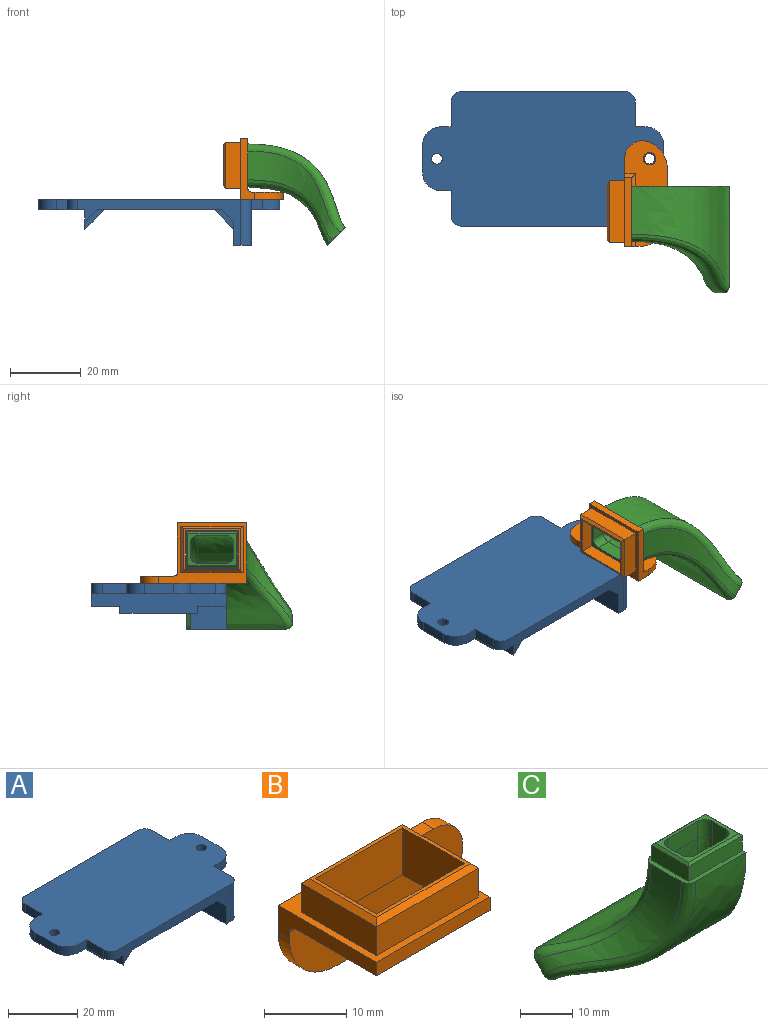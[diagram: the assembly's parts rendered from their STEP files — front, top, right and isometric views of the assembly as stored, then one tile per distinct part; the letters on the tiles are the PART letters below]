
ASSEMBLY  parts=3 mates=4
PART A: 41 faces, bbox 68x38x13 mm
  f0: plane 28x13mm, normal (0,0,-1), area 264.3mm2, adj f16,f17,f18,f19,f20,f21,f22,f23
  f1: plane 38x35mm, normal (0,0,-1), area 1242mm2, adj f2,f3,f13,f23,f29,f30,f31,f32
  f2: plane 8x3.5mm, normal (-0.71,0,-0.71), area 39.6mm2, adj f1,f23,f34,f37
  f3: plane 8x3.5mm, normal (0.71,0,-0.71), area 39.6mm2, adj f1,f23,f28,f31
  f4: plane 38x13mm, normal (0,0,-1), area 312.3mm2, adj f5,f6,f7,f8,f9,f10,f11,f12
  f5: plane 7x3mm, normal (-1,0,0), area 21mm2, adj f4,f6,f25,f27
  f6: plane 3x3mm, normal (0,1,0), area 9mm2, adj f4,f5,f7,f27
  f7: cylinder r=5mm len=5mm, axis (0,0,-1), area 23.6mm2, adj f4,f6,f8,f27
  f8: plane 8x3mm, normal (-1,0,0), area 24mm2, adj f4,f7,f9,f27
  f9: cylinder r=5mm len=5mm, axis (0,0,-1), area 23.6mm2, adj f4,f8,f10,f27
  f10: plane 3x3mm, normal (0,-1,0), area 9mm2, adj f4,f9,f11,f27
  f11: plane 7x3mm, normal (-1,0,0), area 21mm2, adj f4,f10,f12,f27
  f12: cylinder r=3mm len=3mm, axis (0,0,-1), area 14.1mm2, adj f4,f11,f13,f27
  f13: plane 46x13mm, normal (0,-1,0), area 170.2mm2, adj f1,f4,f12,f14,f27,f28,f29,f33
  f14: cylinder r=3mm len=13mm, axis (0,0,-1), area 61.3mm2, adj f13,f15,f27,f40
  f15: plane 13x7mm, normal (1,0,0), area 91mm2, adj f14,f16,f27,f39,f40
  f16: plane 3x3mm, normal (0,-1,0), area 9mm2, adj f0,f15,f17,f27
  f17: cylinder r=5mm len=5mm, axis (0,0,-1), area 23.6mm2, adj f0,f16,f18,f27
  f18: plane 8x3mm, normal (1,0,0), area 24mm2, adj f0,f17,f19,f27
  f19: cylinder r=5mm len=5mm, axis (0,0,-1), area 23.6mm2, adj f0,f18,f20,f27
  f20: plane 3x3mm, normal (0,1,0), area 9mm2, adj f0,f19,f21,f27
  f21: plane 7x3mm, normal (1,0,0), area 21mm2, adj f0,f20,f22,f27
  f22: cylinder r=3mm len=3mm, axis (0,0,-1), area 14.1mm2, adj f0,f21,f23,f27
  f23: plane 46x6.5mm, normal (0,1,0), area 150.3mm2, adj f0,f1,f2,f3,f4,f22,f25,f27
  f24: cylinder r=1.5mm len=3mm, axis (0,0,-1), area 28.3mm2, adj f0,f27
  f25: cylinder r=3mm len=3mm, axis (0,0,-1), area 14.1mm2, adj f4,f5,f23,f27
  f26: cylinder r=1.5mm len=3mm, axis (0,0,-1), area 28.3mm2, adj f4,f27
  f27: plane 68x38mm, normal (0,0,1), area 2220.7mm2, adj f5,f6,f7,f8,f9,f10,f11,f12
  f28: plane 38x5.5mm, normal (-1,0,0), area 177mm2, adj f3,f4,f13,f23,f29,f30,f31,f32
  f29: plane 8x3.5mm, normal (0.71,0,-0.71), area 39.6mm2, adj f1,f13,f28,f30
  f30: plane 5.5x5.5mm, normal (0,-1,0), area 9mm2, adj f1,f28,f29,f32
  f31: plane 5.5x5.5mm, normal (0,1,0), area 9mm2, adj f1,f3,f28,f32
  f32: plane 22x5.5mm, normal (0.71,0,-0.71), area 171.1mm2, adj f1,f28,f30,f31
  f33: plane 8x3.5mm, normal (-0.71,0,-0.71), area 39.6mm2, adj f1,f13,f36,f38
  f34: plane 28x5.5mm, normal (1,0,0), area 138mm2, adj f0,f2,f23,f35,f37,f39
  f35: plane 22x5.5mm, normal (-0.71,0,-0.71), area 171.1mm2, adj f1,f34,f36,f37,f38
  f36: plane 5.5x5.5mm, normal (0,-1,0), area 9mm2, adj f1,f33,f35,f38
  f37: plane 5.5x5.5mm, normal (0,1,0), area 9mm2, adj f1,f2,f34,f35
  f38: plane 10x6.5mm, normal (-1,0,0), area 61mm2, adj f13,f33,f35,f36,f39,f40
  f39: plane 10x5mm, normal (0,1,0), area 50mm2, adj f0,f15,f34,f38,f40
  f40: plane 10x5mm, normal (0,0,-1), area 48.1mm2, adj f13,f14,f15,f38,f39
PART B: 27 faces, bbox 29.8x17x17 mm
  f0: plane 17.5x4.3mm, normal (0,-1,0), area 75.3mm2, adj f1,f3,f9,f23
  f1: plane 13x4.3mm, normal (1,0,0), area 55.9mm2, adj f0,f2,f9,f21
  f2: plane 17.5x4.3mm, normal (0,1,0), area 75.3mm2, adj f1,f3,f9,f22
  f3: plane 13x4.3mm, normal (-1,0,0), area 55.9mm2, adj f0,f2,f9,f24
  f4: plane 16.1x11.6mm, normal (0,0,1), area 26.7mm2, adj f10,f11,f12,f13,f21,f22,f23,f24
  f5: plane 17x4mm, normal (-1,0,0), area 38.2mm2, adj f6,f8,f9,f14,f16,f18,f25
  f6: plane 19.5x2mm, normal (0,-1,0), area 39mm2, adj f5,f7,f8,f9
  f7: plane 14x2mm, normal (1,0,0), area 28mm2, adj f6,f8,f9,f26
  f8: plane 19.5x14mm, normal (0,0,-1), area 112.9mm2, adj f5,f6,f7,f10,f11,f12,f13,f25
  f9: plane 24.83x17mm, normal (0,0,1), area 114.9mm2, adj f0,f1,f2,f3,f5,f6,f7,f14
  f10: plane 15.1x7mm, normal (0,1,0), area 105.7mm2, adj f4,f8,f11,f13
  f11: plane 10.6x7mm, normal (1,0,0), area 74.2mm2, adj f4,f8,f10,f12
  f12: plane 15.1x7mm, normal (0,-1,0), area 105.7mm2, adj f4,f8,f11,f13
  f13: plane 10.6x7mm, normal (-1,0,0), area 74.2mm2, adj f4,f8,f10,f12
  f14: plane 29.83x12mm, normal (0,-1,0), area 255.1mm2, adj f5,f9,f15,f17,f18,f19,f20,f25
  f15: plane 14x2mm, normal (0,0,-1), area 28mm2, adj f14,f16,f18,f19
  f16: plane 29.83x12mm, normal (0,1,0), area 316.6mm2, adj f5,f9,f15,f17,f18,f19,f20
  f17: cylinder r=1.75mm len=3.5mm, axis (0,-1,0), area 22mm2, adj f14,f16
  f18: cylinder r=8mm len=8mm, axis (0,-1,0), area 25.1mm2, adj f5,f14,f15,f16
  f19: cylinder r=8mm len=7.54mm, axis (0,1,0), area 19.7mm2, adj f14,f15,f16,f20
  f20: cylinder r=5mm len=6.67mm, axis (0,1,0), area 19.1mm2, adj f9,f14,f16,f19
  f21: plane 13x0.7mm, normal (0.71,0,0.71), area 12.2mm2, adj f1,f4,f22,f23
  f22: plane 17.5x0.7mm, normal (0,0.71,0.71), area 16.6mm2, adj f2,f4,f21,f24
  f23: plane 17.5x0.7mm, normal (0,-0.71,0.71), area 16.6mm2, adj f0,f4,f21,f24
  f24: plane 13x0.7mm, normal (-0.71,0,0.71), area 12.2mm2, adj f3,f4,f22,f23
  f25: cylinder r=1mm len=20.5mm, axis (1,0,0), area 31.2mm2, adj f5,f8,f14,f26
  f26: cylinder r=1mm len=3mm, axis (0,0,1), area 3.7mm2, adj f7,f9,f14,f25
PART C: 31 faces, bbox 30.1x28.7x47.8 mm
  f0: plane 14.6x3.5mm, normal (0,-1,0), area 51.1mm2, adj f1,f7,f12,f16
  f1: plane 30.98x28.53mm, normal (1,0,0), area 369mm2, adj f0,f2,f10,f13,f15,f16,f17
  f2: plane 14.6x3.5mm, normal (0,1,0), area 51.1mm2, adj f1,f7,f9,f16
  f3: plane 4x3.7mm, normal (1,0,0), area 14.8mm2, adj f8,f19,f22,f24
  f4: plane 8.2x4mm, normal (0,-1,0), area 32.8mm2, adj f8,f20,f22,f28
  f5: plane 29.22x22.07mm, normal (-1,0,0), area 88.7mm2, adj f8,f17,f25,f26,f27,f28
  f6: plane 8.2x4mm, normal (0,1,0), area 32.8mm2, adj f8,f18,f24,f26
  f7: plane 10.1x3.5mm, normal (-1,0,0), area 35.3mm2, adj f0,f2,f11,f16
  f8: plane 13.6x9.1mm, normal (0,0,1), area 33.3mm2, adj f3,f4,f5,f6,f9,f10,f11,f12
  f9: plane 14.6x0.5mm, normal (0,0.71,0.71), area 10mm2, adj f2,f8,f10,f11
  f10: plane 10.1x0.5mm, normal (0.71,0,0.71), area 6.8mm2, adj f1,f8,f9,f12
  f11: plane 10.1x0.5mm, normal (-0.71,0,0.71), area 6.8mm2, adj f7,f8,f9,f12
  f12: plane 14.6x0.5mm, normal (0,-0.71,0.71), area 10mm2, adj f0,f8,f10,f11
  f13: bspline ~30x27.48mm, area 736mm2, adj f1,f16,f17,f29
  f14: bspline ~28.53x27.48mm, area 207.2mm2, adj f16,f17,f29,f30
  f15: bspline ~30x22.53mm, area 581.8mm2, adj f1,f16,f17,f30
  f16: plane 15.66x12.16mm, normal (0,0,1), area 39.6mm2, adj f0,f1,f2,f7,f13,f14,f15,f29
  f17: plane 30.06x5.01mm, normal (0,0.71,-0.71), area 84.8mm2, adj f1,f5,f13,f14,f15,f18,f19,f20
  f18: bspline ~27.6x26.63mm, area 508.4mm2, adj f6,f17,f23,f25
  f19: bspline ~26.63x25.48mm, area 75.9mm2, adj f3,f17,f21,f23
  f20: bspline ~27.6x23.37mm, area 454.1mm2, adj f4,f17,f21,f27
  f21: bspline ~25.96x19.87mm, area 101.7mm2, adj f17,f19,f20,f22
  f22: cylinder r=2mm len=4mm, axis (0,0,1), area 12.6mm2, adj f3,f4,f8,f21
  f23: bspline ~27.68x23.69mm, area 148.8mm2, adj f17,f18,f19,f24
  f24: cylinder r=2mm len=4mm, axis (0,0,-1), area 12.6mm2, adj f3,f6,f8,f23
  f25: bspline ~46.98x23.77mm, area 118mm2, adj f5,f17,f18,f26
  f26: cylinder r=2mm len=4mm, axis (0,0,1), area 12.6mm2, adj f5,f6,f8,f25
  f27: bspline ~28.98x19.9mm, area 103.1mm2, adj f5,f17,f20,f28
  f28: cylinder r=2mm len=4mm, axis (0,0,-1), area 12.6mm2, adj f4,f5,f8,f27
  f29: bspline ~28.52x25.05mm, area 151.7mm2, adj f13,f14,f16,f17
  f30: bspline ~24.23x18.5mm, area 96.7mm2, adj f14,f15,f16,f17
PLACE A t=(0.03,0.03,3.52)mm fixed
PLACE B rot(axis=(-0.58,-0.58,0.58),120deg) t=(18.03,-14.97,16.02)mm
PLACE C rot(axis=(-0.58,-0.58,0.58),120deg) t=(25.03,-14.99,16.02)mm
MATE parallel B.f9 <-> A.f8  axis (-1,0,0) through (23.03,-13.8,12.33)mm
MATE planar B.f16 <-> A.f27  axis (0,0,-1) through (28.72,-10.29,6.52)mm
MATE cylindrical B.f17 <-> A.f24  axis (0,0,1) through (30.03,0.03,8.52)mm
MATE planar C.f16 <-> B.f8  axis (-1,0,0) through (25.03,-23.29,16.02)mm
